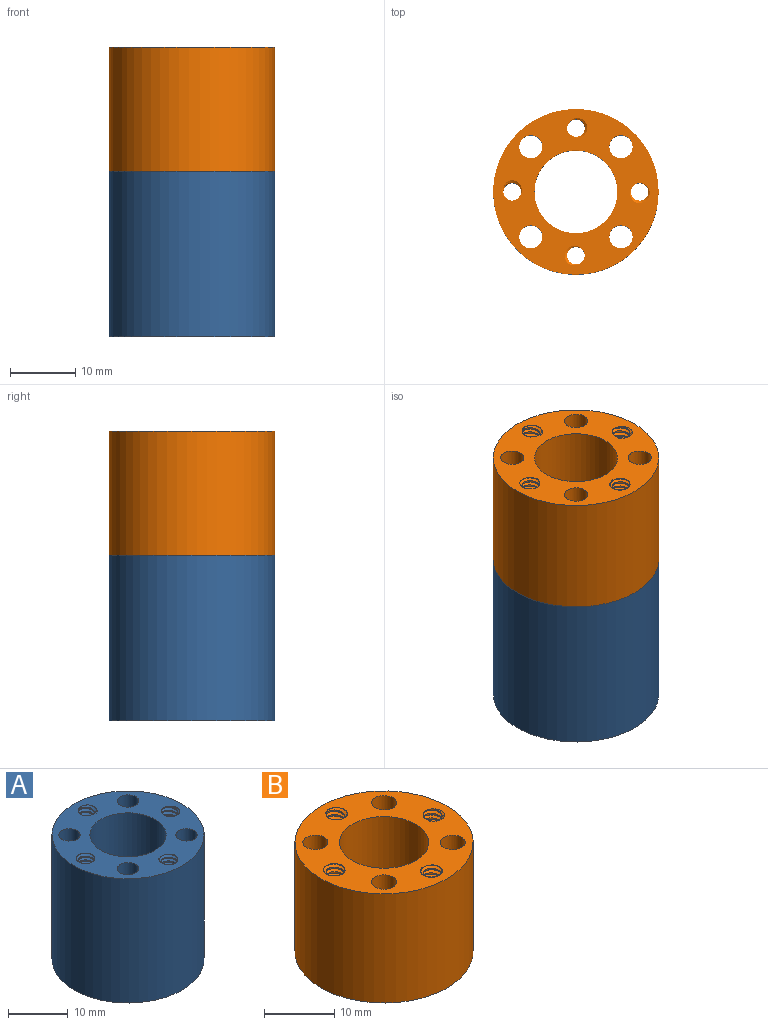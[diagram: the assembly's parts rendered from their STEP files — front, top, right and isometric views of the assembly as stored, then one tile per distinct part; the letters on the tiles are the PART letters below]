
ASSEMBLY  parts=2 mates=1
PART A: 24 faces, bbox 25.6x25.6x26.1 mm
  f0: cylinder r=1.75mm len=25.4mm, axis (0,0,1), area 35mm2, adj f14,f15,f22,f23
  f1: cylinder r=1.75mm len=25.4mm, axis (0,0,1), area 35mm2, adj f14,f15,f20,f21
  f2: cylinder r=1.75mm len=25.4mm, axis (0,0,1), area 35mm2, adj f14,f15,f18,f19
  f3: cylinder r=1.75mm len=25.4mm, axis (0,0,1), area 35mm2, adj f14,f15,f16,f17
  f4: cylinder r=1.35mm len=25.4mm, axis (0,0,-1), area 63.3mm2, adj f14,f15,f18,f19
  f5: cylinder r=1.35mm len=25.4mm, axis (0,0,-1), area 63.3mm2, adj f14,f15,f16,f17
  f6: cylinder r=1.35mm len=25.4mm, axis (0,0,-1), area 63.3mm2, adj f14,f15,f22,f23
  f7: cylinder r=1.35mm len=25.4mm, axis (0,0,-1), area 63.3mm2, adj f14,f15,f20,f21
  f8: cylinder r=1.78mm len=25.4mm, axis (0,0,-1), area 283.8mm2, adj f14,f15
  f9: cylinder r=1.78mm len=25.4mm, axis (0,0,-1), area 283.8mm2, adj f14,f15
  f10: cylinder r=1.78mm len=25.4mm, axis (0,0,-1), area 283.8mm2, adj f14,f15
  f11: cylinder r=1.78mm len=25.4mm, axis (0,0,-1), area 283.8mm2, adj f14,f15
  f12: cylinder r=6.36mm len=25.4mm, axis (0,0,-1), area 1015.4mm2, adj f14,f15
  f13: cylinder r=12.7mm len=25.4mm, axis (0,0,-1), area 2026.2mm2, adj f14,f15
  f14: plane 25.58x25.58mm, normal (0,0,1), area 310.2mm2, adj f0,f1,f2,f3,f4,f5,f6,f7
  f15: plane 25.58x25.58mm, normal (0,0,-1), area 310.2mm2, adj f0,f1,f2,f3,f4,f5,f6,f7
  f16: bspline ~25.86x3.5mm, area 144.6mm2, adj f3,f5,f14,f15
  f17: bspline ~25.86x3.51mm, area 144.6mm2, adj f3,f5,f14,f15
  f18: bspline ~25.86x3.5mm, area 144.6mm2, adj f2,f4,f14,f15
  f19: bspline ~25.86x3.51mm, area 144.6mm2, adj f2,f4,f14,f15
  f20: bspline ~25.86x3.5mm, area 144.6mm2, adj f1,f7,f14,f15
  f21: bspline ~25.86x3.51mm, area 144.6mm2, adj f1,f7,f14,f15
  f22: bspline ~25.86x3.5mm, area 144.6mm2, adj f0,f6,f14,f15
  f23: bspline ~25.86x3.51mm, area 144.6mm2, adj f0,f6,f14,f15
PART B: 24 faces, bbox 25.6x25.6x19.7 mm
  f0: cylinder r=1.75mm len=19.05mm, axis (0,0,1), area 26.2mm2, adj f14,f15,f22,f23
  f1: cylinder r=1.75mm len=19.05mm, axis (0,0,1), area 26.2mm2, adj f14,f15,f20,f21
  f2: cylinder r=1.75mm len=19.05mm, axis (0,0,1), area 26.2mm2, adj f14,f15,f18,f19
  f3: cylinder r=1.75mm len=19.05mm, axis (0,0,1), area 26.2mm2, adj f14,f15,f16,f17
  f4: cylinder r=1.35mm len=19.05mm, axis (0,0,-1), area 47.4mm2, adj f14,f15,f16,f17
  f5: cylinder r=1.35mm len=19.05mm, axis (0,0,-1), area 47.4mm2, adj f14,f15,f18,f19
  f6: cylinder r=1.35mm len=19.05mm, axis (0,0,-1), area 47.4mm2, adj f14,f15,f22,f23
  f7: cylinder r=1.35mm len=19.05mm, axis (0,0,-1), area 47.4mm2, adj f14,f15,f20,f21
  f8: cylinder r=1.78mm len=19.05mm, axis (0,0,-1), area 212.8mm2, adj f14,f15
  f9: cylinder r=1.78mm len=19.05mm, axis (0,0,-1), area 212.8mm2, adj f14,f15
  f10: cylinder r=1.78mm len=19.05mm, axis (0,0,-1), area 212.8mm2, adj f14,f15
  f11: cylinder r=1.78mm len=19.05mm, axis (0,0,-1), area 212.8mm2, adj f14,f15
  f12: cylinder r=6.36mm len=19.05mm, axis (0,0,-1), area 761.6mm2, adj f14,f15
  f13: cylinder r=12.7mm len=25.39mm, axis (0,0,-1), area 1519.7mm2, adj f14,f15
  f14: plane 25.58x25.58mm, normal (0,0,-1), area 310.2mm2, adj f0,f1,f2,f3,f4,f5,f6,f7
  f15: plane 25.58x25.58mm, normal (0,0,1), area 310.2mm2, adj f0,f1,f2,f3,f4,f5,f6,f7
  f16: bspline ~19.51x3.51mm, area 108.4mm2, adj f3,f4,f14,f15
  f17: bspline ~19.51x3.51mm, area 108.4mm2, adj f3,f4,f14,f15
  f18: bspline ~19.51x3.51mm, area 108.4mm2, adj f2,f5,f14,f15
  f19: bspline ~19.51x3.51mm, area 108.4mm2, adj f2,f5,f14,f15
  f20: bspline ~19.51x3.51mm, area 108.4mm2, adj f1,f7,f14,f15
  f21: bspline ~19.51x3.51mm, area 108.4mm2, adj f1,f7,f14,f15
  f22: bspline ~19.51x3.51mm, area 108.4mm2, adj f0,f6,f14,f15
  f23: bspline ~19.51x3.51mm, area 108.4mm2, adj f0,f6,f14,f15
PLACE A t=(-0.02,0.08,-12.56)mm
PLACE B t=(-0.02,0.08,12.84)mm
MATE fastened B.f10 <-> A.f10  axis (0,0,-1) through (6.9,7,12.84)mm
